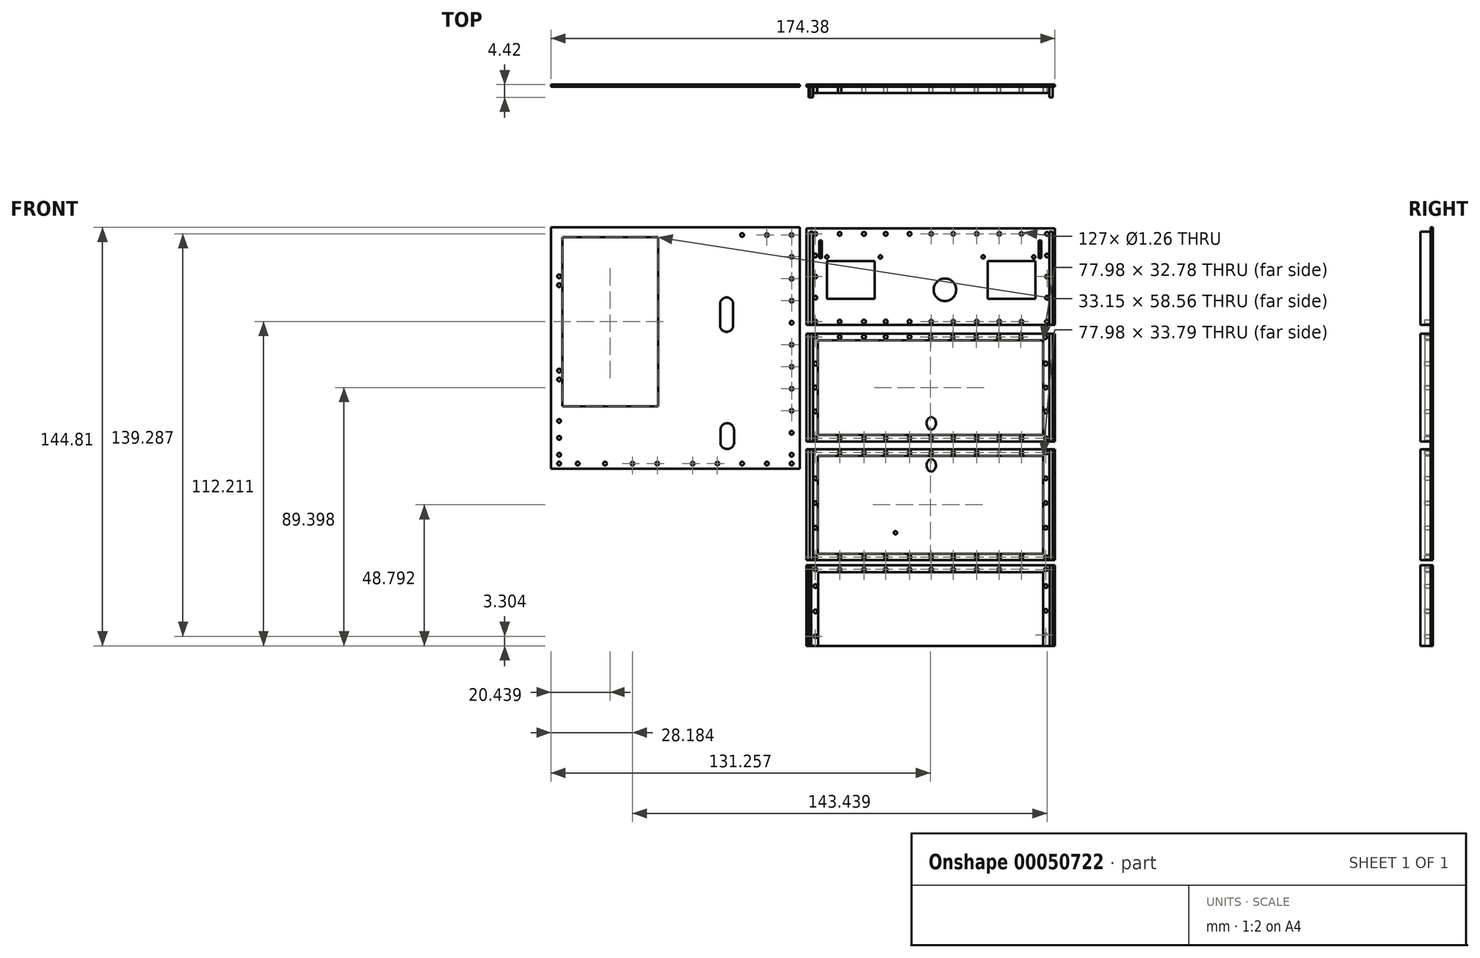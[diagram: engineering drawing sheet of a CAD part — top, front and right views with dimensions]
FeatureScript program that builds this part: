
annotation { "Feature Type Name" : "Feature", "Feature Type Description" : "" }
export const myFeature = defineFeature(function(context is Context, id is Id, definition is map)
    precondition{}
    {
        {
            var Q0;
            Q0=qCreatedBy(makeId("Front.planeOp"),FACE);
            var sketch = newSketch(context, id + "F0", { "sketchPlane" : qUnion([Q0])});
            skLineSegment(sketch, "E0", {"start": v(60.4, -32.47) * mm, "end": v(60.4, 4.87) * mm});
            skLineSegment(sketch, "E1", {"start": v(-25.65, 4.87) * mm, "end": v(-25.65, -32.47) * mm});
            skCircle(sketch, "E2", {"center": v(-22.51, 3.72) * mm, "radius": 0.63 * mm});
            skCircle(sketch, "E3", {"center": v(-22.51, -31.32) * mm, "radius": 0.63 * mm});
            skCircle(sketch, "E4", {"center": v(10.08, 3.73) * mm, "radius": 0.65 * mm});
            skPoint(sketch, "E4.centerSnap0", {"position": v(16.45, -32.47) * mm});
            skCircle(sketch, "E5", {"center": v(57.07, 3.63) * mm, "radius": 0.65 * mm});
            skLineSegment(sketch, "E6.trimOffspring", {"start": v(56.44, -12.15) * mm, "end": v(56.44, -12.15) * mm});
            skCircle(sketch, "E7", {"center": v(-14.12, 3.73) * mm, "radius": 0.63 * mm});
            skCircle(sketch, "E8", {"center": v(-5.7, 3.73) * mm, "radius": 0.68 * mm});
            skCircle(sketch, "E9", {"center": v(1.84, 3.73) * mm, "radius": 0.67 * mm});
            skCircle(sketch, "E10", {"center": v(-14.12, -31.33) * mm, "radius": 0.63 * mm});
            skCircle(sketch, "E11", {"center": v(-5.7, -31.33) * mm, "radius": 0.63 * mm});
            skCircle(sketch, "E12", {"center": v(1.84, -31.33) * mm, "radius": 0.63 * mm});
            skCircle(sketch, "E13", {"center": v(17.58, -31.33) * mm, "radius": 0.63 * mm});
            skCircle(sketch, "E14", {"center": v(41.12, -31.33) * mm, "radius": 0.63 * mm});
            skCircle(sketch, "E15", {"center": v(48.81, -31.33) * mm, "radius": 0.63 * mm});
            skCircle(sketch, "E16", {"center": v(48.62, 3.63) * mm, "radius": 0.63 * mm});
            skCircle(sketch, "E17", {"center": v(40.93, 3.63) * mm, "radius": 0.63 * mm});
            skCircle(sketch, "E18", {"center": v(17.39, 3.63) * mm, "radius": 0.63 * mm});
            skLineSegment(sketch, "E19.MirrorCS", {"start": v(56.44, -55.55) * mm, "end": v(56.44, -55.55) * mm});
            skCircle(sketch, "E20.MirrorC", {"center": v(-22.51, -36.37) * mm, "radius": 0.63 * mm});
            skCircle(sketch, "E21.MirrorC", {"center": v(41.12, -36.37) * mm, "radius": 0.63 * mm});
            skCircle(sketch, "E22.MirrorC", {"center": v(-14.1, -36.37) * mm, "radius": 0.63 * mm});
            skCircle(sketch, "E23.MirrorC", {"center": v(1.84, -36.37) * mm, "radius": 0.63 * mm});
            skCircle(sketch, "E24.MirrorC", {"center": v(17.58, -36.37) * mm, "radius": 0.63 * mm});
            skCircle(sketch, "E25.MirrorC", {"center": v(48.81, -36.37) * mm, "radius": 0.63 * mm});
            skCircle(sketch, "E26.MirrorC", {"center": v(-5.7, -36.37) * mm, "radius": 0.63 * mm});
            skPoint(sketch, "E27.MirrorP", {"position": v(16.45, -35.23) * mm});
            skLineSegment(sketch, "E28", {"start": v(60.4, -35.23) * mm, "end": v(60.4, -73.58) * mm});
            skLineSegment(sketch, "E29", {"start": v(-25.65, -73.58) * mm, "end": v(-25.65, -35.23) * mm});
            skCircle(sketch, "E30", {"center": v(10.07, -31.33) * mm, "radius": 0.63 * mm});
            skCircle(sketch, "E31", {"center": v(-22.51, -13.78) * mm, "radius": 0.65 * mm});
            skCircle(sketch, "E32", {"center": v(-22.51, -5.51) * mm, "radius": 0.67 * mm});
            skCircle(sketch, "E33", {"center": v(-22.51, -22.06) * mm, "radius": 0.65 * mm});
            skCircle(sketch, "E34.MirrorC", {"center": v(57.26, -31.33) * mm, "radius": 0.63 * mm});
            skCircle(sketch, "E35.MirrorC", {"center": v(57.26, -22.07) * mm, "radius": 0.65 * mm});
            skCircle(sketch, "E36.MirrorC", {"center": v(57.26, -13.78) * mm, "radius": 0.65 * mm});
            skCircle(sketch, "E37.MirrorC", {"center": v(57.26, -5.52) * mm, "radius": 0.67 * mm});
            skCircle(sketch, "E38.MirrorC", {"center": v(10.07, -36.37) * mm, "radius": 0.63 * mm});
            skCircle(sketch, "E39.MirrorC", {"center": v(57.26, -36.37) * mm, "radius": 0.63 * mm});
            skCircle(sketch, "E40.MirrorC", {"center": v(-22.51, -72.48) * mm, "radius": 0.63 * mm});
            skCircle(sketch, "E41.MirrorC", {"center": v(-14.1, -72.44) * mm, "radius": 0.63 * mm});
            skCircle(sketch, "E42.MirrorC", {"center": v(-5.7, -72.44) * mm, "radius": 0.63 * mm});
            skCircle(sketch, "E43.MirrorC", {"center": v(1.84, -72.44) * mm, "radius": 0.63 * mm});
            skCircle(sketch, "E44.MirrorC", {"center": v(10.07, -72.44) * mm, "radius": 0.63 * mm});
            skCircle(sketch, "E45.MirrorC", {"center": v(17.58, -72.44) * mm, "radius": 0.63 * mm});
            skCircle(sketch, "E46.MirrorC", {"center": v(41.12, -72.44) * mm, "radius": 0.63 * mm});
            skCircle(sketch, "E47.MirrorC", {"center": v(48.81, -72.44) * mm, "radius": 0.63 * mm});
            skCircle(sketch, "E48.MirrorC", {"center": v(57.26, -72.44) * mm, "radius": 0.63 * mm});
            skCircle(sketch, "E49", {"center": v(-22.51, -53.78) * mm, "radius": 0.64 * mm});
            skCircle(sketch, "E50", {"center": v(-22.51, -45.25) * mm, "radius": 0.64 * mm});
            skCircle(sketch, "E51.MirrorC", {"center": v(-22.51, -62.31) * mm, "radius": 0.64 * mm});
            skCircle(sketch, "E52.MirrorC", {"center": v(57.25, -53.77) * mm, "radius": 0.64 * mm});
            skCircle(sketch, "E53.MirrorC", {"center": v(57.25, -45.24) * mm, "radius": 0.64 * mm});
            skCircle(sketch, "E54.MirrorC", {"center": v(57.25, -62.3) * mm, "radius": 0.64 * mm});
            skCircle(sketch, "E55.MirrorC", {"center": v(57.26, -76.78) * mm, "radius": 0.63 * mm});
            skCircle(sketch, "E56.MirrorC", {"center": v(48.81, -76.75) * mm, "radius": 0.63 * mm});
            skCircle(sketch, "E57.MirrorC", {"center": v(41.12, -76.75) * mm, "radius": 0.63 * mm});
            skCircle(sketch, "E58.MirrorC", {"center": v(17.58, -76.75) * mm, "radius": 0.63 * mm});
            skCircle(sketch, "E59.MirrorC", {"center": v(10.07, -76.75) * mm, "radius": 0.63 * mm});
            skCircle(sketch, "E60.MirrorC", {"center": v(-22.51, -76.75) * mm, "radius": 0.63 * mm});
            skCircle(sketch, "E61.MirrorC", {"center": v(-14.1, -76.75) * mm, "radius": 0.63 * mm});
            skCircle(sketch, "E62.MirrorC", {"center": v(-5.7, -76.75) * mm, "radius": 0.63 * mm});
            skCircle(sketch, "E63.MirrorC", {"center": v(1.84, -76.75) * mm, "radius": 0.63 * mm});
            skLineSegment(sketch, "E64", {"start": v(-25.65, -75.36) * mm, "end": v(-25.65, -103.2) * mm});
            skLineSegment(sketch, "E65", {"start": v(60.4, -75.36) * mm, "end": v(60.4, -103.2) * mm});
            skCircle(sketch, "E66.MirrorC", {"center": v(-22.51, -99.9) * mm, "radius": 0.63 * mm});
            skCircle(sketch, "E67.MirrorC", {"center": v(57.26, -99.41) * mm, "radius": 0.63 * mm});
            skCircle(sketch, "E68", {"center": v(-22.51, -82.51) * mm, "radius": 0.64 * mm});
            skCircle(sketch, "E69", {"center": v(-22.51, -91.28) * mm, "radius": 0.64 * mm});
            skCircle(sketch, "E70.MirrorC", {"center": v(57.26, -91.1) * mm, "radius": 0.64 * mm});
            skCircle(sketch, "E71.MirrorC", {"center": v(57.26, -82.51) * mm, "radius": 0.64 * mm});
            skCircle(sketch, "E72.MirrorC", {"center": v(-22.51, 9.03) * mm, "radius": 0.63 * mm});
            skCircle(sketch, "E73.MirrorC", {"center": v(-14.12, 9.02) * mm, "radius": 0.63 * mm});
            skCircle(sketch, "E74.MirrorC", {"center": v(-5.7, 9.02) * mm, "radius": 0.68 * mm});
            skCircle(sketch, "E75.MirrorC", {"center": v(1.84, 9.02) * mm, "radius": 0.67 * mm});
            skCircle(sketch, "E76.MirrorC", {"center": v(10.07, 9.02) * mm, "radius": 0.65 * mm});
            skCircle(sketch, "E77.MirrorC", {"center": v(17.58, 9.02) * mm, "radius": 0.63 * mm});
            skCircle(sketch, "E78.MirrorC", {"center": v(25.2, 9.02) * mm, "radius": 0.63 * mm});
            skCircle(sketch, "E79.MirrorC", {"center": v(48.81, 9.02) * mm, "radius": 0.63 * mm});
            skCircle(sketch, "E80.MirrorC", {"center": v(57.64, 9.02) * mm, "radius": 0.65 * mm});
            skLineSegment(sketch, "E81", {"start": v(-25.65, 7.89) * mm, "end": v(-25.65, 41.33) * mm});
            skLineSegment(sketch, "E82", {"start": v(60.4, 7.89) * mm, "end": v(60.4, 41.33) * mm});
            skCircle(sketch, "E83.MirrorC", {"center": v(-22.51, 39.38) * mm, "radius": 0.63 * mm});
            skCircle(sketch, "E84.MirrorC", {"center": v(-14.12, 39.4) * mm, "radius": 0.63 * mm});
            skCircle(sketch, "E85.MirrorC", {"center": v(-5.7, 39.4) * mm, "radius": 0.68 * mm});
            skCircle(sketch, "E86.MirrorC", {"center": v(1.84, 39.4) * mm, "radius": 0.67 * mm});
            skCircle(sketch, "E87.MirrorC", {"center": v(10.07, 39.4) * mm, "radius": 0.65 * mm});
            skCircle(sketch, "E88.MirrorC", {"center": v(17.58, 39.4) * mm, "radius": 0.63 * mm});
            skCircle(sketch, "E89.MirrorC", {"center": v(25.2, 39.4) * mm, "radius": 0.63 * mm});
            skCircle(sketch, "E90.MirrorC", {"center": v(48.81, 39.4) * mm, "radius": 0.63 * mm});
            skCircle(sketch, "E91.MirrorC", {"center": v(57.64, 39.4) * mm, "radius": 0.65 * mm});
            skCircle(sketch, "E92", {"center": v(-22.51, 24.6) * mm, "radius": 0.63 * mm});
            skCircle(sketch, "E93", {"center": v(-22.51, 31.91) * mm, "radius": 0.64 * mm});
            skCircle(sketch, "E94.MirrorC", {"center": v(-22.51, 17.3) * mm, "radius": 0.64 * mm});
            skCircle(sketch, "E95.MirrorC", {"center": v(57.64, 31.91) * mm, "radius": 0.64 * mm});
            skCircle(sketch, "E96.MirrorC", {"center": v(57.64, 24.6) * mm, "radius": 0.63 * mm});
            skCircle(sketch, "E97.MirrorC", {"center": v(57.64, 17.3) * mm, "radius": 0.64 * mm});
            skLineSegment(sketch, "E98", {"start": v(-18.51, 30.04) * mm, "end": v(-2, 30.04) * mm});
            skLineSegment(sketch, "E99", {"start": v(-2, 30.04) * mm, "end": v(-2, 16.93) * mm});
            skLineSegment(sketch, "E100", {"start": v(-2, 16.93) * mm, "end": v(-18.51, 16.93) * mm});
            skLineSegment(sketch, "E101", {"start": v(-18.51, 16.93) * mm, "end": v(-18.51, 30.04) * mm});
            skLineSegment(sketch, "E102.MirrorCS", {"start": v(53.65, 30.04) * mm, "end": v(37.14, 30.04) * mm});
            skLineSegment(sketch, "E103.MirrorCS", {"start": v(37.14, 30.04) * mm, "end": v(37.14, 16.93) * mm});
            skLineSegment(sketch, "E104.MirrorCS", {"start": v(37.14, 16.93) * mm, "end": v(53.65, 16.93) * mm});
            skLineSegment(sketch, "E105.MirrorCS", {"start": v(53.65, 16.93) * mm, "end": v(53.65, 30.04) * mm});
            skCircle(sketch, "E106", {"center": v(22.32, 20.03) * mm, "radius": 3.9 * mm});
            skEllipse(sketch, "E107", {"center": v(17.58, -40.74) * mm, "majorRadius": 2.16 * mm, "minorRadius": 1.63 * mm, "majorAxis": v(0, -1)});
            skCircle(sketch, "E108.MirrorC", {"center": v(33.33, 9.02) * mm, "radius": 0.63 * mm});
            skCircle(sketch, "E109.MirrorC", {"center": v(33.33, 39.4) * mm, "radius": 0.63 * mm});
            skCircle(sketch, "E110.MirrorC", {"center": v(41.12, 9.02) * mm, "radius": 0.63 * mm});
            skCircle(sketch, "E111.MirrorC", {"center": v(41.12, 39.4) * mm, "radius": 0.63 * mm});
            skCircle(sketch, "E112", {"center": v(33.33, -31.33) * mm, "radius": 0.63 * mm});
            skCircle(sketch, "E113", {"center": v(33.13, 3.63) * mm, "radius": 0.63 * mm});
            skCircle(sketch, "E114", {"center": v(25.2, -31.33) * mm, "radius": 0.63 * mm});
            skCircle(sketch, "E115", {"center": v(25.01, 3.63) * mm, "radius": 0.63 * mm});
            skCircle(sketch, "E116.MirrorC", {"center": v(25.2, -36.37) * mm, "radius": 0.63 * mm});
            skCircle(sketch, "E117.MirrorC", {"center": v(33.33, -36.37) * mm, "radius": 0.63 * mm});
            skCircle(sketch, "E118.MirrorC", {"center": v(33.33, -72.44) * mm, "radius": 0.63 * mm});
            skCircle(sketch, "E119.MirrorC", {"center": v(25.2, -72.44) * mm, "radius": 0.63 * mm});
            skEllipse(sketch, "E120", {"center": v(17.58, -26.17) * mm, "majorRadius": 2.16 * mm, "minorRadius": 1.63 * mm, "majorAxis": v(0, -1)});
            skCircle(sketch, "E121.MirrorC", {"center": v(25.2, -76.75) * mm, "radius": 0.63 * mm});
            skCircle(sketch, "E122.MirrorC", {"center": v(33.33, -76.75) * mm, "radius": 0.63 * mm});
            skLineSegment(sketch, "E123", {"start": v(55.68, 37.12) * mm, "end": v(55.68, 30.95) * mm});
            skLineSegment(sketch, "E124", {"start": v(55.68, 30.95) * mm, "end": v(54.76, 30.95) * mm});
            skLineSegment(sketch, "E125", {"start": v(54.76, 30.95) * mm, "end": v(54.76, 37.12) * mm});
            skLineSegment(sketch, "E126", {"start": v(54.76, 37.12) * mm, "end": v(55.68, 37.12) * mm});
            skLineSegment(sketch, "E127", {"start": v(-20.2, 37.12) * mm, "end": v(-20.2, 30.95) * mm});
            skLineSegment(sketch, "E128", {"start": v(-20.2, 30.95) * mm, "end": v(-21.13, 30.95) * mm});
            skLineSegment(sketch, "E129", {"start": v(-21.13, 30.95) * mm, "end": v(-21.13, 37.12) * mm});
            skLineSegment(sketch, "E130", {"start": v(-21.13, 37.12) * mm, "end": v(-20.2, 37.12) * mm});
            skCircle(sketch, "E131", {"center": v(53.09, 31.4) * mm, "radius": 0.57 * mm});
            skCircle(sketch, "E132", {"center": v(35.57, 31.4) * mm, "radius": 0.57 * mm});
            skCircle(sketch, "E133", {"center": v(0, 31.4) * mm, "radius": 0.57 * mm});
            skCircle(sketch, "E134", {"center": v(-18.53, 31.4) * mm, "radius": 0.57 * mm});
            skLineSegment(sketch, "E135", {"start": v(61.66, 37.87) * mm, "end": v(62.8, 37.87) * mm});
            skLineSegment(sketch, "E136", {"start": v(-29.02, 40.47) * mm, "end": v(-30.16, 40.47) * mm});
            skLineSegment(sketch, "E137", {"start": v(-22.51, -75.95) * mm, "end": v(-22.51, -77.54) * mm});
            skLineSegment(sketch, "E138", {"start": v(56.27, 38.59) * mm, "end": v(56.27, 10.16) * mm});
            skLineSegment(sketch, "E139", {"start": v(-21.71, 38.59) * mm, "end": v(-21.71, 10.17) * mm});
            skLineSegment(sketch, "E140", {"start": v(-21.71, 2.59) * mm, "end": v(-21.71, -30.2) * mm});
            skLineSegment(sketch, "E141", {"start": v(-21.71, -37.51) * mm, "end": v(-21.71, -71.3) * mm});
            skLineSegment(sketch, "E142", {"start": v(-21.52, -77.71) * mm, "end": v(-21.52, -103.2) * mm});
            skLineSegment(sketch, "E143", {"start": v(-23.3, 38.59) * mm, "end": v(-23.3, 7.89) * mm});
            skLineSegment(sketch, "E144.trimOffspring", {"start": v(-23.9, -75.36) * mm, "end": v(-23.9, -103.2) * mm});
            skLineSegment(sketch, "E145.trimOffspring", {"start": v(-23.3, 4.87) * mm, "end": v(-23.3, -32.47) * mm});
            skLineSegment(sketch, "E146.trimOffspring", {"start": v(-23.3, -35.23) * mm, "end": v(-23.3, -73.58) * mm});
            skLineSegment(sketch, "E147", {"start": v(56.27, 2.59) * mm, "end": v(56.27, -30.2) * mm});
            skLineSegment(sketch, "E148", {"start": v(58.44, 38.59) * mm, "end": v(58.44, 7.89) * mm});
            skLineSegment(sketch, "E149.trimOffspring", {"start": v(58.65, -75.36) * mm, "end": v(58.65, -103.2) * mm});
            skLineSegment(sketch, "E150.trimOffspring", {"start": v(58.44, -35.23) * mm, "end": v(58.44, -73.58) * mm});
            skLineSegment(sketch, "E151.trimOffspring", {"start": v(58.44, 4.87) * mm, "end": v(58.44, -32.47) * mm});
            skLineSegment(sketch, "E152", {"start": v(-24.45, 40.18) * mm, "end": v(-24.45, 7.89) * mm});
            skLineSegment(sketch, "E153.trimOffspring", {"start": v(-24.9, -75.36) * mm, "end": v(-24.9, -103.2) * mm});
            skLineSegment(sketch, "E154.trimOffspring", {"start": v(-24.45, 4.87) * mm, "end": v(-24.45, -32.47) * mm});
            skLineSegment(sketch, "E155.trimOffspring", {"start": v(-24.45, -35.23) * mm, "end": v(-24.45, -73.58) * mm});
            skLineSegment(sketch, "E156", {"start": v(59.58, 40.19) * mm, "end": v(59.58, 7.89) * mm});
            skLineSegment(sketch, "E157.trimOffspring", {"start": v(59.58, 4.87) * mm, "end": v(59.58, -32.47) * mm});
            skLineSegment(sketch, "E158.trimOffspring", {"start": v(59.58, -35.23) * mm, "end": v(59.58, -73.58) * mm});
            skLineSegment(sketch, "E159.trimOffspring", {"start": v(59.64, -75.36) * mm, "end": v(59.64, -103.2) * mm});
            skLineSegment(sketch, "E160", {"start": v(58.44, 38.59) * mm, "end": v(58.44, 40.19) * mm});
            skLineSegment(sketch, "E161", {"start": v(-23.3, 38.59) * mm, "end": v(-23.3, 40.18) * mm});
            skLineSegment(sketch, "E162", {"start": v(-27.28, -89.05) * mm, "end": v(-29.67, -89.05) * mm});
            skLineSegment(sketch, "E163", {"start": v(-29.67, -90.1) * mm, "end": v(-30.66, -90.1) * mm});
            skLineSegment(sketch, "E164", {"start": v(-30.66, -89.05) * mm, "end": v(-31.41, -89.05) * mm});
            skLineSegment(sketch, "E165", {"start": v(42.02, -64.53) * mm, "end": v(42.02, -66.91) * mm});
            skCircle(sketch, "E166", {"center": v(5.2, -64.07) * mm, "radius": 0.57 * mm});
            skLineSegment(sketch, "E167", {"start": v(-32.67, -98.28) * mm, "end": v(-32.67, -99.88) * mm});
            skLineSegment(sketch, "E168", {"start": v(-32.67, -99.88) * mm, "end": v(-32.67, -101.02) * mm});
            skLineSegment(sketch, "E169", {"start": v(-32.67, -101.02) * mm, "end": v(-32.67, -101.84) * mm});
            skLineSegment(sketch, "E170", {"start": v(-25.65, -112.9) * mm, "end": v(56.97, -112.9) * mm});
            skLineSegment(sketch, "E171", {"start": v(-25.65, -103.2) * mm, "end": v(-25.65, -112.9) * mm});
            skLineSegment(sketch, "E172", {"start": v(-25.65, -109.3) * mm, "end": v(60.4, -109.3) * mm});
            skLineSegment(sketch, "E173", {"start": v(-25.65, 4.87) * mm, "end": v(60.4, 4.87) * mm});
            skLineSegment(sketch, "E174", {"start": v(-25.65, -32.47) * mm, "end": v(60.4, -32.47) * mm});
            skLineSegment(sketch, "E175", {"start": v(-25.65, -35.23) * mm, "end": v(60.4, -35.23) * mm});
            skLineSegment(sketch, "E176", {"start": v(-25.65, -73.58) * mm, "end": v(60.4, -73.58) * mm});
            skLineSegment(sketch, "E177", {"start": v(-25.65, -103.2) * mm, "end": v(60.4, -103.2) * mm});
            skLineSegment(sketch, "E178", {"start": v(-25.65, -75.36) * mm, "end": v(60.4, -75.36) * mm});
            skLineSegment(sketch, "E179", {"start": v(-21.52, -77.71) * mm, "end": v(56.27, -77.71) * mm});
            skLineSegment(sketch, "E180", {"start": v(56.27, -77.71) * mm, "end": v(56.27, -103.2) * mm});
            skLineSegment(sketch, "E181", {"start": v(-25.65, 7.89) * mm, "end": v(60.4, 7.89) * mm});
            skLineSegment(sketch, "E182", {"start": v(-21.71, 10.17) * mm, "end": v(56.27, 10.16) * mm});
            skLineSegment(sketch, "E183", {"start": v(-25.65, 41.33) * mm, "end": v(60.4, 41.33) * mm});
            skLineSegment(sketch, "E184", {"start": v(-24.45, 40.18) * mm, "end": v(59.58, 40.19) * mm});
            skLineSegment(sketch, "E185", {"start": v(-21.71, 38.59) * mm, "end": v(56.27, 38.59) * mm});
            skLineSegment(sketch, "E186", {"start": v(-21.71, 2.59) * mm, "end": v(56.27, 2.59) * mm});
            skPoint(sketch, "E187.startSnap0", {"position": v(-18.12, 3.73) * mm});
            skLineSegment(sketch, "E188", {"start": v(-21.71, -30.2) * mm, "end": v(56.27, -30.2) * mm});
            skPoint(sketch, "E189.orphan", {"position": v(-21.71, -32.47) * mm});
            skPoint(sketch, "E190.startSnap0", {"position": v(-16.88, -31.33) * mm});
            skLineSegment(sketch, "E191", {"start": v(-21.71, -37.51) * mm, "end": v(56.27, -37.51) * mm});
            skPoint(sketch, "E192.orphan", {"position": v(-21.71, -35.23) * mm});
            skLineSegment(sketch, "E193.trimOffspring", {"start": v(56.27, -37.51) * mm, "end": v(56.27, -71.3) * mm});
            skLineSegment(sketch, "E194", {"start": v(-21.71, -71.3) * mm, "end": v(56.27, -71.3) * mm});
            skPoint(sketch, "E195.orphan", {"position": v(56.27, -73.58) * mm});
            skSolve(sketch);
        }
        {
            var Q0;
            Q0 = qSketchRegion(id + "F0", true);
            var Q1;
            Q1=makeQuery(id+"F0.imprint","IMPRINT",FACE,{"disambiguationData":[TD([[makeQuery(id+"F0.imprint","IMPRINT",EDGE,{"derivedFrom":sQuery(id+"F0.wireOp",EDGE,"E98")}),1.0]])]});
            var Q2;
            Q2=makeQuery(id+"F0.imprint","IMPRINT",FACE,{"disambiguationData":[TD([[makeQuery(id+"F0.imprint","IMPRINT",EDGE,{"derivedFrom":sQuery(id+"F0.wireOp",EDGE,"E107")}),-1.0]])]});
            var Q3;
            Q3=makeQuery(id+"F0.imprint","IMPRINT",FACE,{"disambiguationData":[TD([[makeQuery(id+"F0.imprint","IMPRINT",EDGE,{"derivedFrom":sQuery(id+"F0.wireOp",EDGE,"E120")}),-1.0]])]});
            extrude(context, id + "F1", {"entities" : qUnion([Q0, Q1, Q2, Q3]), "depth" : 0.76 * mm, "offsetDistance" : 25.4 * mm});
        }
        {
            var Q0;
            Q0=qCreatedBy(makeId("Front.planeOp"),FACE);
            var sketch = newSketch(context, id + "F2", { "sketchPlane" : qUnion([Q0])});
            skLineSegment(sketch, "E196", {"start": v(-113.98, 41.61) * mm, "end": v(-113.98, -41.9) * mm});
            skLineSegment(sketch, "E197", {"start": v(-27.93, 41.61) * mm, "end": v(-27.93, -41.9) * mm});
            skLineSegment(sketch, "E198", {"start": v(-51.05, 15.74) * mm, "end": v(-51.05, 7) * mm});
            skLineSegment(sketch, "E199", {"start": v(-55.4, 7) * mm, "end": v(-55.4, 15.74) * mm});
            skArc(sketch, "E200", {"start": v(-51.05, 15.74) * mm, "mid": v(-53.22, 17.38) * mm, "end": v(-55.4, 15.74) * mm});
            skArc(sketch, "E201", {"start": v(-55.4, 7) * mm, "mid": v(-53.22, 5.5) * mm, "end": v(-51.05, 7) * mm});
            skLineSegment(sketch, "E202", {"start": v(-110.11, -20.27) * mm, "end": v(-76.97, -20.27) * mm});
            skLineSegment(sketch, "E203", {"start": v(-76.97, -20.27) * mm, "end": v(-76.97, 38.29) * mm});
            skLineSegment(sketch, "E204", {"start": v(-76.97, 38.29) * mm, "end": v(-110.11, 38.29) * mm});
            skLineSegment(sketch, "E205", {"start": v(-110.11, 38.29) * mm, "end": v(-110.11, -20.27) * mm});
            skLineSegment(sketch, "E206", {"start": v(-55.34, -28.45) * mm, "end": v(-55.34, -33.36) * mm});
            skLineSegment(sketch, "E207", {"start": v(-50.69, -33.36) * mm, "end": v(-50.69, -28.45) * mm});
            skArc(sketch, "E208", {"start": v(-50.69, -28.45) * mm, "mid": v(-53.02, -26.12) * mm, "end": v(-55.34, -28.45) * mm});
            skArc(sketch, "E209", {"start": v(-55.34, -33.36) * mm, "mid": v(-53.02, -35.08) * mm, "end": v(-50.69, -33.36) * mm});
            skCircle(sketch, "E210.MirrorC", {"center": v(-30.74, 38.99) * mm, "radius": 0.63 * mm});
            skCircle(sketch, "E211.MirrorC", {"center": v(-111.19, -31.22) * mm, "radius": 0.67 * mm});
            skCircle(sketch, "E212.MirrorC", {"center": v(-30.72, -40.13) * mm, "radius": 0.65 * mm});
            skCircle(sketch, "E213.MirrorC", {"center": v(-47.85, 38.99) * mm, "radius": 0.65 * mm});
            skCircle(sketch, "E214.MirrorC", {"center": v(-39.28, 38.99) * mm, "radius": 0.63 * mm});
            skCircle(sketch, "E215.MirrorC", {"center": v(-30.72, -14.22) * mm, "radius": 0.63 * mm});
            skCircle(sketch, "E216.MirrorC", {"center": v(-30.72, -37.07) * mm, "radius": 0.65 * mm});
            skCircle(sketch, "E217.MirrorC", {"center": v(-30.72, -29.46) * mm, "radius": 0.65 * mm});
            skLineSegment(sketch, "E218", {"start": v(-18.2, 56.85) * mm, "end": v(-18.2, 49.03) * mm});
            skCircle(sketch, "E219.MirrorC", {"center": v(-39.28, -40.13) * mm, "radius": 0.65 * mm});
            skCircle(sketch, "E220.MirrorC", {"center": v(-30.72, -21.84) * mm, "radius": 0.63 * mm});
            skCircle(sketch, "E221.MirrorC", {"center": v(-30.72, 16.23) * mm, "radius": 0.63 * mm});
            skCircle(sketch, "E222.MirrorC", {"center": v(-47.85, -40.13) * mm, "radius": 0.65 * mm});
            skCircle(sketch, "E223.MirrorC", {"center": v(-64.97, -40.13) * mm, "radius": 0.63 * mm});
            skCircle(sketch, "E224.MirrorC", {"center": v(-56.4, -40.13) * mm, "radius": 0.63 * mm});
            skCircle(sketch, "E225.MirrorC", {"center": v(-30.72, 8.61) * mm, "radius": 0.65 * mm});
            skCircle(sketch, "E226.MirrorC", {"center": v(-30.72, 1) * mm, "radius": 0.63 * mm});
            skCircle(sketch, "E227.MirrorC", {"center": v(-30.72, 23.84) * mm, "radius": 0.63 * mm});
            skCircle(sketch, "E228.MirrorC", {"center": v(-111.19, -25.36) * mm, "radius": 0.65 * mm});
            skCircle(sketch, "E229.MirrorC", {"center": v(-30.72, -6.61) * mm, "radius": 0.63 * mm});
            skCircle(sketch, "E230.MirrorC", {"center": v(-30.72, 31.45) * mm, "radius": 0.63 * mm});
            skCircle(sketch, "E231.MirrorC", {"center": v(-111.19, -40.13) * mm, "radius": 0.65 * mm});
            skCircle(sketch, "E232.MirrorC", {"center": v(-111.19, -37.07) * mm, "radius": 0.65 * mm});
            skCircle(sketch, "E233.MirrorC", {"center": v(-104.76, -40.13) * mm, "radius": 0.65 * mm});
            skCircle(sketch, "E234.MirrorC", {"center": v(-95.28, -40.13) * mm, "radius": 0.65 * mm});
            skCircle(sketch, "E235.MirrorC", {"center": v(-85.8, -40.13) * mm, "radius": 0.63 * mm});
            skCircle(sketch, "E236.MirrorC", {"center": v(-77.23, -40.13) * mm, "radius": 0.63 * mm});
            skCircle(sketch, "E237.MirrorC", {"center": v(-111.19, -11.02) * mm, "radius": 0.65 * mm});
            skCircle(sketch, "E238.MirrorC", {"center": v(-111.19, -7.96) * mm, "radius": 0.65 * mm});
            skCircle(sketch, "E239.MirrorC", {"center": v(-111.19, 21.64) * mm, "radius": 0.65 * mm});
            skCircle(sketch, "E240.MirrorC", {"center": v(-111.19, 24.7) * mm, "radius": 0.65 * mm});
            skLineSegment(sketch, "E241", {"start": v(-113.98, -46.77) * mm, "end": v(-27.93, -46.77) * mm});
            skLineSegment(sketch, "E242", {"start": v(-113.98, -41.9) * mm, "end": v(-113.98, -46.77) * mm});
            skLineSegment(sketch, "E243", {"start": v(-113.98, -41.9) * mm, "end": v(-27.93, -41.9) * mm});
            skLineSegment(sketch, "E244", {"start": v(-113.98, 41.61) * mm, "end": v(-27.93, 41.61) * mm});
            skLineSegment(sketch, "E245", {"start": v(-27.93, -40.9) * mm, "end": v(-29.13, -40.9) * mm});
            skLineSegment(sketch, "E246", {"start": v(-29.13, -40.9) * mm, "end": v(-30.27, -40.9) * mm});
            skLineSegment(sketch, "E247", {"start": v(-30.27, -40.9) * mm, "end": v(-31.87, -40.9) * mm});
            skSolve(sketch);
        }
        {
            var Q0;
            Q0 = qSketchRegion(id + "F2", true);
            extrude(context, id + "F3", {"entities" : qUnion([Q0]), "depth" : 0.76 * mm, "offsetDistance" : 25.4 * mm});
        }
        {
            var Q0;
            {var subQ1=sQuery(id+"F0.wireOp",EDGE,"E143");Q0=makeQuery(id+"F0.imprint","IMPRINT",FACE,{"disambiguationData":[TD([[makeQuery(id+"F0.imprint","IMPRINT",EDGE,{"derivedFrom":subQ1}),-1.0]])]});}
            var Q1;
            {var subQ0=sQuery(id+"F0.wireOp",EDGE,"E145.trimOffspring");Q1=makeQuery(id+"F0.imprint","IMPRINT",FACE,{"disambiguationData":[TD([[makeQuery(id+"F0.imprint","IMPRINT",EDGE,{"derivedFrom":subQ0}),-1.0]])]});}
            var Q2;
            {var subQ3=sQuery(id+"F0.wireOp",EDGE,"E148");Q2=makeQuery(id+"F0.imprint","IMPRINT",FACE,{"disambiguationData":[TD([[makeQuery(id+"F0.imprint","IMPRINT",EDGE,{"derivedFrom":subQ3}),1.0]])]});}
            var Q3;
            {var subQ0=sQuery(id+"F0.wireOp",EDGE,"E151.trimOffspring");Q3=makeQuery(id+"F0.imprint","IMPRINT",FACE,{"disambiguationData":[TD([[makeQuery(id+"F0.imprint","IMPRINT",EDGE,{"derivedFrom":subQ0}),1.0]])]});}
            var Q4;
            {var subQ0=sQuery(id+"F0.wireOp",EDGE,"E149.trimOffspring");Q4=makeQuery(id+"F0.imprint","IMPRINT",FACE,{"disambiguationData":[TD([[makeQuery(id+"F0.imprint","IMPRINT",EDGE,{"derivedFrom":subQ0}),1.0]])]});}
            var Q5;
            {var subQ0=sQuery(id+"F0.wireOp",EDGE,"E150.trimOffspring");Q5=makeQuery(id+"F0.imprint","IMPRINT",FACE,{"disambiguationData":[TD([[makeQuery(id+"F0.imprint","IMPRINT",EDGE,{"derivedFrom":subQ0}),1.0]])]});}
            var Q6;
            {var subQ0=sQuery(id+"F0.wireOp",EDGE,"E146.trimOffspring");Q6=makeQuery(id+"F0.imprint","IMPRINT",FACE,{"disambiguationData":[TD([[makeQuery(id+"F0.imprint","IMPRINT",EDGE,{"derivedFrom":subQ0}),-1.0]])]});}
            var Q7;
            {var subQ0=sQuery(id+"F0.wireOp",EDGE,"E144.trimOffspring");Q7=makeQuery(id+"F0.imprint","IMPRINT",FACE,{"disambiguationData":[TD([[makeQuery(id+"F0.imprint","IMPRINT",EDGE,{"derivedFrom":subQ0}),-1.0]])]});}
            extrude(context, id + "F4", {"entities" : qUnion([Q0, Q1, Q2, Q3, Q4, Q5, Q6, Q7]), "depth" : 4.42 * mm, "offsetDistance" : 25.4 * mm});
        }
        {
            var Q0;
            Q0=makeQuery(id+"F0.imprint","IMPRINT",FACE,{"disambiguationData":[TD([[makeQuery(id+"F0.imprint","IMPRINT",EDGE,{"derivedFrom":sQuery(id+"F0.wireOp",EDGE,"E56.MirrorC")}),1.0]])]});
            var Q1;
            Q1=makeQuery(id+"F0.imprint","IMPRINT",FACE,{"disambiguationData":[TD([[makeQuery(id+"F0.imprint","IMPRINT",EDGE,{"derivedFrom":sQuery(id+"F0.wireOp",EDGE,"E41.MirrorC")}),-1.0]])]});
            var Q2;
            Q2=makeQuery(id+"F0.imprint","IMPRINT",FACE,{"disambiguationData":[TD([[makeQuery(id+"F0.imprint","IMPRINT",EDGE,{"derivedFrom":sQuery(id+"F0.wireOp",EDGE,"E21.MirrorC")}),1.0]])]});
            var Q3;
            Q3=makeQuery(id+"F0.imprint","IMPRINT",FACE,{"disambiguationData":[TD([[makeQuery(id+"F0.imprint","IMPRINT",EDGE,{"derivedFrom":sQuery(id+"F0.wireOp",EDGE,"E10")}),-1.0]])]});
            var Q4;
            Q4=makeQuery(id+"F0.imprint","IMPRINT",FACE,{"disambiguationData":[TD([[makeQuery(id+"F0.imprint","IMPRINT",EDGE,{"derivedFrom":sQuery(id+"F0.wireOp",EDGE,"E4")}),-1.0]])]});
            var Q5;
            Q5=makeQuery(id+"F0.imprint","IMPRINT",FACE,{"disambiguationData":[TD([[makeQuery(id+"F0.imprint","IMPRINT",EDGE,{"derivedFrom":sQuery(id+"F0.wireOp",EDGE,"E73.MirrorC")}),1.0]])]});
            var Q6;
            Q6=makeQuery(id+"F0.imprint","IMPRINT",FACE,{"disambiguationData":[TD([[makeQuery(id+"F0.imprint","IMPRINT",EDGE,{"derivedFrom":sQuery(id+"F0.wireOp",EDGE,"E72.MirrorC")}),1.0]])]});
            var Q7;
            Q7=makeQuery(id+"F0.imprint","IMPRINT",FACE,{"disambiguationData":[TD([[makeQuery(id+"F0.imprint","IMPRINT",EDGE,{"derivedFrom":sQuery(id+"F0.wireOp",EDGE,"E67.MirrorC")}),1.0]])]});
            var Q8;
            Q8=makeQuery(id+"F0.imprint","IMPRINT",FACE,{"disambiguationData":[TD([[makeQuery(id+"F0.imprint","IMPRINT",EDGE,{"derivedFrom":sQuery(id+"F0.wireOp",EDGE,"E39.MirrorC")}),-1.0]])]});
            var Q9;
            Q9=makeQuery(id+"F0.imprint","IMPRINT",FACE,{"disambiguationData":[TD([[makeQuery(id+"F0.imprint","IMPRINT",EDGE,{"derivedFrom":sQuery(id+"F0.wireOp",EDGE,"E66.MirrorC")}),-1.0]])]});
            var Q10;
            Q10=makeQuery(id+"F0.imprint","IMPRINT",FACE,{"disambiguationData":[TD([[makeQuery(id+"F0.imprint","IMPRINT",EDGE,{"derivedFrom":sQuery(id+"F0.wireOp",EDGE,"E20.MirrorC")}),1.0]])]});
            var Q11;
            Q11=makeQuery(id+"F0.imprint","IMPRINT",FACE,{"disambiguationData":[TD([[makeQuery(id+"F0.imprint","IMPRINT",EDGE,{"derivedFrom":sQuery(id+"F0.wireOp",EDGE,"E2")}),-1.0]])]});
            var Q12;
            Q12=makeQuery(id+"F0.imprint","IMPRINT",FACE,{"disambiguationData":[TD([[makeQuery(id+"F0.imprint","IMPRINT",EDGE,{"derivedFrom":sQuery(id+"F0.wireOp",EDGE,"E5")}),-1.0]])]});
            extrude(context, id + "F5", {"entities" : qUnion([Q0, Q1, Q2, Q3, Q4, Q5, Q6, Q7, Q8, Q9, Q10, Q11, Q12]), "depth" : 2.82 * mm, "offsetDistance" : 25.4 * mm});
        }
    });
